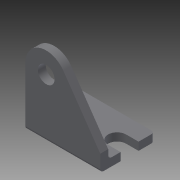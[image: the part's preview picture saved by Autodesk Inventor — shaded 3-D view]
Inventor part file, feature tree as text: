
AUTODESK INVENTOR PART (.ipt)
format: ipt  version: 2014 (Build 180170000, 170)  size: 147,456 bytes
history: native  units: in
note: dims shown in document units (in); Inventor stores cm internally (conversion verified against a paired STEP export)
features: other x14, sketch x8, extrude x5, hole x3
ambient origin geometry x8: Origin, YZ Plane, XZ Plane, XY Plane, X Axis, Y Axis, Z Axis, Center Point
bodies: Solid1 (feature_tree)
feature tree (30):
  extrude  "Extrusion1"  Depth=0.817in TaperAngle=0.0deg
  extrude  "Extrusion2"  Depth=0.1196in TaperAngle=0.0deg
  hole  "Hole1"  [1 undecoded]
  hole  "Hole2"  [1 undecoded]
  hole  "Hole3"  [1 undecoded]
  sketch  "Sketch_6"
  sketch  "Sketch_7"
  extrude  "Extrusion3"  [1 undecoded]
  extrude  "Extrusion4"  [1 undecoded]
  extrude  "Extrusion5"  [1 undecoded]
  other  "to_dummy_R_XY"
  other  "to_dummy_R_YZ"
  other  "to_dummy_R_ZX"
  other  "to_dummy_R_X"
  other  "to_dummy_R_Y"
  other  "to_dummy_R_Z"
  other  "to_dummy_R_Center"
  other  "to_pin_R_XY"
  other  "to_pin_R_YZ"
  other  "to_pin_R_ZX"
  other  "to_pin_R_X"
  other  "to_pin_R_Y"
  other  "to_pin_R_Z"
  other  "to_pin_R_Center"
  sketch  "Sketch_1"  dims[d0=1.125in d1=0.0in d2=0.817in d3=0.0in]
  sketch  "Sketch_2"  dims[d4=0.2528in d5=0.75in d6=0.375in d7=0.25in d8=0.5635in d9=0.1196in d10=0.0in]
  sketch  "Sketch3"  dims[d11=0.27in d12=0.75in d13=0.375in d14=0.25in d15=0.5635in d16=0.1196in d17=0.0in]
  sketch  "Sketch4"  dims[d18=0.27in d19=0.75in d20=0.375in d21=0.25in d22=0.5635in d23=0.1196in d24=0.0in d25=0.1196in d26=0.0in]
  sketch  "Sketch5"  dims[d27=0.1196in d28=0.0in d29=0.1196in d30=0.0in]
  sketch  "Sketch_8"
note: 6 required parameter values undecoded (feature->parameter linkage not recoverable at this tier; creation-order binding heuristic only, values carry confidence <= 0.55)
